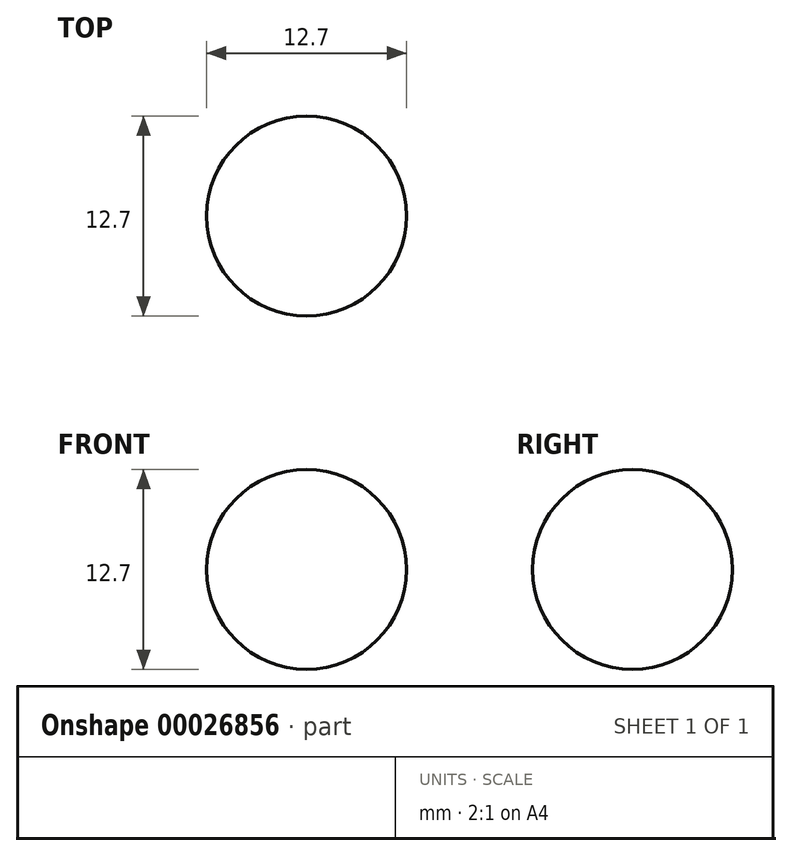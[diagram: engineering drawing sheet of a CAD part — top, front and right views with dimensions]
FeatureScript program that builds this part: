
annotation { "Feature Type Name" : "Feature", "Feature Type Description" : "" }
export const myFeature = defineFeature(function(context is Context, id is Id, definition is map)
    precondition{}
    {
        {
            var Q0;
            Q0=qCreatedBy(makeId("Front.planeOp"),FACE);
            var sketch = newSketch(context, id + "F0", { "sketchPlane" : qUnion([Q0])});
            skArc(sketch, "E0", {"start": v(0, -6.35) * mm, "mid": v(6.35, 0) * mm, "end": v(0, 6.35) * mm});
            skLineSegment(sketch, "E1", {"start": v(0, 6.35) * mm, "end": v(0, -6.35) * mm});
            skSolve(sketch);
        }
        {
            var Q0;
            Q0=makeQuery(id+"F0.imprint","IMPRINT",FACE,{"disambiguationData":[TD([[makeQuery(id+"F0.imprint","IMPRINT",EDGE,{"derivedFrom":sQuery(id+"F0.wireOp",EDGE,"E0")}),1.0]])]});
            var Q1;
            Q1=sQuery(id+"F0.wireOp",EDGE,"E1");
            revolve(context, id + "F1", {"entities" : qUnion([Q0]), "axis" : qUnion([Q1]), "revolveType" : RevolveType.FULL});
        }
    });
